# Revit family: Gira_216200
name_source: partatom
category: Elektroinstallationen
revit_build: Autodesk Revit 2017 (Build: 20160225_1515(x64)
units: mm (PartAtom-declared; Revit-internal decimal feet)

## family parameters
Basisbauteil = Fläche
Beim Laden mit Abzugskörper schneiden = Nein
Bemaßung runder Anschluss = Durchmesser verwenden
Beschriftungsausrichtung beibehalten = Nein
Gemeinsam genutzt = Nein
Raumberechnungspunkt = Nein
Teiletyp = Normal

## types (1)
- Raumaktor KNX REG
    Andere Bussysteme = ohne
    Anzahl der Ausgänge = 0
    Anzahl der Eingänge = 0
    Anzahl der binären Eingänge = 0
    BIM = https://media.stage.bim.site 8f.rfa
    BIMSITE_PRODUCT_ID = a7ec78d93201e89a0426071e1eb0df07dd7cfba7
    Beschreibung = KNX Raumaktor  REG plus Merkmale:  Der Raumaktor steuert in einem Gerät drei verschiedene Gewerke, wie Beleuchtung, Jalousie und Heizung. Die vier Relaisausgänge lassen sich in der ETS (Engineering Tool Software) entweder auf Jalousiebetrieb oder Schaltbetrieb einstellen, auch ein Mischbetrieb ist möglich.  Zwei Schaltausgänge ergeben einen Jalousieausgang.  Zusätzlich sind zwei weitere elektronische Schaltausgänge für die Ansteuerung von Stellantrieben vorhanden. Schaltbetrieb:  Der Raumaktor steuert mit seinen Relaiskontakten elektrische Verbraucher wie bspw. Beleuchtungsanlagen. Die Relaiskontakte sind bistabil, so dass der zuletzt eingestellte Schaltzustand auch bei Ausfall der Versorgungsspannung unverändert bleibt.  Funktionseigenschaften je Ausgang: umfangreiche Zeitfunktionen, logische Verknüpfungen, Szenen, Sperrfunktionen oder alternativ Zwangsführungen, erweiterte Rückmeldungen, eine zyklische Überwachung der eintreffenden Schalttelegramme sowie einen Betriebsstundenzähler. Jalousiebetrieb:  Der Raumaktor steuert mit seinen Relaiskontakten elektrisch betriebene Jalousien, Rollläden, Markisen, Lüftungsklappen oder ähnliche Behänge mit einer Netzspannung von AC 230 V.  Funktionseigenschaften für jeden Ausgangskanal: separat parametrierbare Fahrzeiten, erweiterte Rückmeldefunktionen, Zuordnungen auf bis zu fünf verschiedene Sicherheitsfunktionen, eine umfangreiche Sonnenschutzfunktion und die Einbindung in Szenen oder Zwangsführungen. Raumtemperaturregelung:  Zwei zusätzliche elektronische Schaltausgänge dienen der geräuschlosen Ansteuerung von elektrothermischen Stellantrieben für Heiz- oder Kühlanlagen.  Stetige Stellgrößentelegramme werden in ein pulsweitenmoduliertes Ausgangssignal (PWM) umgesetzt. Dadurch können die Stellantriebe stetig angesteuert werden. Alternativ ist die Umsetzung von schaltenden Stellgrößen möglich. Statusmeldung für die Ventilstellung und die zyklische Überwachung der Stellgrößentelegramme.  Notbetrieb bei Busspannungsausfall oder Bus- und Netzspannungswiederkehr plus Zwangsstellung über Bustelegramm im Sommer- und Winterbetrieb.  Alarmmeldung bei Kurzschluss oder Überlast des Schaltausgangs und Festsitzschutz für die Ventile. Es können stromlos geschlossene oder geöffnete Ventilantriebe angeschlossen werden.  Überwachung der Netzspannungsversorgung und damit im Störfall die Aussendung einer Alarmmeldung auf den Bus.  Sammelmeldungen alle Ventile geschlossen" und "größte Stellgröße".  Hinweise :  VDE-Zulassung gemäß EN 60669-1, EN 60669-2-1.  Montage auf DIN-Hutschiene."
    Blindleistung = Nein
    Breite in Teilungseinheiten = 4
    Busspannung pufferbar = Nein
    Bussystem Funkbus = Nein
    Bussystem KNX = Ja
    Bussystem KNX-Funk = Nein
    Bussystem LON = Nein
    Bussystem Powernet = Nein
    Datenblatt = https://media.stage.bim.site
    Datenblatt 1 = https://media.stage.bim.site
    Funktion Schalten = Ja
    GTIN = 4010337059370
    Geeignet für C-Last = Nein
    HAN = 216200
    Handschaltung = Nein
    HeinzeBIM = https://www.heinze.de
    Hersteller = Gira
    Kosten = 0 $
    LED ansteuern = Nein
    Max. Anzahl der Jalousieausgänge = 0
    Max. Anzahl der Schaltausgänge = 0
    Max. Schaltstrom = 2300 A
    Mit Busankopplung = Nein
    Mit LED-Anzeige = Nein
    Modulare Erweiterungsmöglichkeit = Nein
    Montageart = REG
    Produktseite = https://media.stage.bim.site
    Schutzart (IP) = IP20
    Stellgröße schaltend = Nein
    Stellgröße stetig = Nein
    Stromart = AC
    Tarifumschaltung = Nein
    Typname = Raumaktor KNX REG
    URL = https://www.gira.de
    Ventilschutzfunktion = Nein
    Verschiedene Phasen anschließbar = Nein
    Vor Ort-/Handbedienung = Nein
    Vorgabe-Ansicht = 1219 mm
    Zulassung nach PTB = Nein

## geometry (parser evidence)
native form markers: Sweep x3
no freeform markers — native parametric forms only
